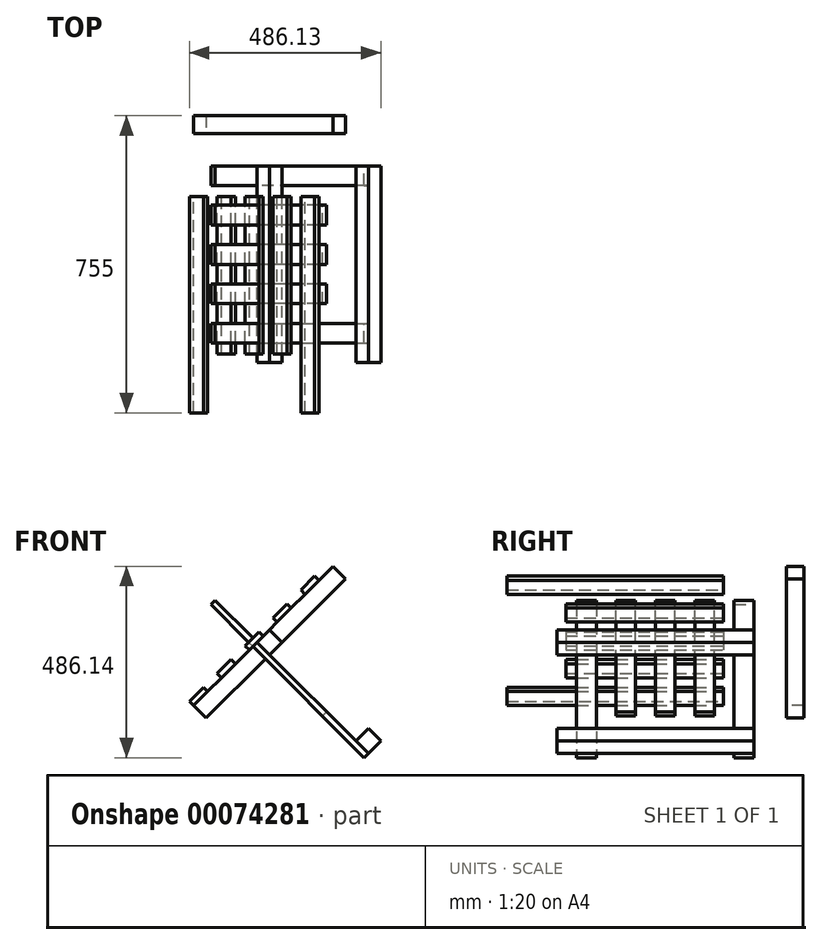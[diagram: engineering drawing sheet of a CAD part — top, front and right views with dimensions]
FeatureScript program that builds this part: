
annotation { "Feature Type Name" : "Feature", "Feature Type Description" : "" }
export const myFeature = defineFeature(function(context is Context, id is Id, definition is map)
    precondition{}
    {
        {
            var Q0;
            Q0=qCreatedBy(makeId("Front.planeOp"),FACE);
            var sketch = newSketch(context, id + "F0", { "sketchPlane" : qUnion([Q0])});
            skLineSegment(sketch, "E0.rect.bottom", {"start": v(0, 31.82) * mm, "end": v(31.82, 0) * mm});
            skLineSegment(sketch, "E0.rect.top", {"start": v(-31.82, 0) * mm, "end": v(0, -31.82) * mm});
            skLineSegment(sketch, "E0.rect.left", {"start": v(0, 31.82) * mm, "end": v(-31.82, 0) * mm});
            skLineSegment(sketch, "E0.rect.right", {"start": v(31.82, 0) * mm, "end": v(0, -31.82) * mm});
            skPoint(sketch, "E0.rect.middle", {"position": v(0, 0) * mm});
            skLineSegment(sketch, "E1", {"start": v(-57.8, 0) * mm, "end": v(51.56, 0) * mm, "construction": true});
            skSolve(sketch);
        }
        {
            var Q0;
            Q0=makeQuery(id+"F0.imprint","IMPRINT",FACE,{"disambiguationData":[TD([[makeQuery(id+"F0.imprint","IMPRINT",EDGE,{"derivedFrom":sQuery(id+"F0.wireOp",EDGE,"E0.rect.bottom")}),-1.0]])]});
            extrude(context, id + "F1", {"entities" : qUnion([Q0]), "endBound" : BoundingType.SYMMETRIC, "depth" : 500 * mm});
        }
        {
            var Q0;
            Q0=makeQuery(id+"F1.opExtrude","SWEPT_FACE",FACE,{"disambiguationData":[OSD([sQuery(id+"F0.wireOp",EDGE,"E0.rect.left")])]});
            var sketch = newSketch(context, id + "F2", { "sketchPlane" : qUnion([Q0])});
            skLineSegment(sketch, "E2.bottom", {"start": v(227.5, -200) * mm, "end": v(-172.5, -200) * mm});
            skLineSegment(sketch, "E2.top", {"start": v(227.5, -250) * mm, "end": v(-172.5, -250) * mm});
            skLineSegment(sketch, "E2.left", {"start": v(227.5, -200) * mm, "end": v(227.5, -250) * mm});
            skLineSegment(sketch, "E2.right", {"start": v(-172.5, -200) * mm, "end": v(-172.5, -250) * mm});
            skLineSegment(sketch, "E3.0.1.0", {"start": v(-172.5, -100) * mm, "end": v(-172.5, -150) * mm});
            skLineSegment(sketch, "E3.0.1.1", {"start": v(227.5, -100) * mm, "end": v(227.5, -150) * mm});
            skLineSegment(sketch, "E3.0.1.2", {"start": v(227.5, -150) * mm, "end": v(-172.5, -150) * mm});
            skLineSegment(sketch, "E3.0.1.3", {"start": v(227.5, -100) * mm, "end": v(-172.5, -100) * mm});
            skLineSegment(sketch, "E3.0.2.0", {"start": v(-172.5, 0) * mm, "end": v(-172.5, -50) * mm});
            skLineSegment(sketch, "E3.0.2.1", {"start": v(227.5, 0) * mm, "end": v(227.5, -50) * mm});
            skLineSegment(sketch, "E3.0.2.2", {"start": v(227.5, -50) * mm, "end": v(-172.5, -50) * mm});
            skLineSegment(sketch, "E3.0.2.3", {"start": v(227.5, 0) * mm, "end": v(-172.5, 0) * mm});
            skLineSegment(sketch, "E3.0.3.0", {"start": v(-172.5, 100) * mm, "end": v(-172.5, 50) * mm});
            skLineSegment(sketch, "E3.0.3.1", {"start": v(227.5, 100) * mm, "end": v(227.5, 50) * mm});
            skLineSegment(sketch, "E3.0.3.2", {"start": v(227.5, 50) * mm, "end": v(-172.5, 50) * mm});
            skLineSegment(sketch, "E3.0.3.3", {"start": v(227.5, 100) * mm, "end": v(-172.5, 100) * mm});
            skLineSegment(sketch, "E3.0.4.0", {"start": v(-172.5, 200) * mm, "end": v(-172.5, 150) * mm});
            skLineSegment(sketch, "E3.0.4.1", {"start": v(227.5, 200) * mm, "end": v(227.5, 150) * mm});
            skLineSegment(sketch, "E3.0.4.2", {"start": v(227.5, 150) * mm, "end": v(-172.5, 150) * mm});
            skLineSegment(sketch, "E3.0.4.3", {"start": v(227.5, 200) * mm, "end": v(-172.5, 200) * mm});
            skLineSegment(sketch, "E3.direction1", {"start": v(-172.5, -250) * mm, "end": v(-172.5, -250) * mm});
            skLineSegment(sketch, "E3.direction2", {"start": v(-172.5, -250) * mm, "end": v(-172.5, -150) * mm, "construction": true});
            skLineSegment(sketch, "E4.bottom", {"start": v(227.5, -200) * mm, "end": v(377.5, -200) * mm});
            skLineSegment(sketch, "E4.top", {"start": v(227.5, -250) * mm, "end": v(377.5, -250) * mm});
            skLineSegment(sketch, "E4.right", {"start": v(377.5, -200) * mm, "end": v(377.5, -250) * mm});
            skLineSegment(sketch, "E5.bottom", {"start": v(227.5, 200) * mm, "end": v(377.5, 200) * mm});
            skLineSegment(sketch, "E5.top", {"start": v(227.5, 150) * mm, "end": v(377.5, 150) * mm});
            skLineSegment(sketch, "E5.right", {"start": v(377.5, 200) * mm, "end": v(377.5, 150) * mm});
            skSolve(sketch);
        }
        {
            var Q0;
            {var subQ0=sQuery(id+"F2.wireOp",EDGE,"E2.left");Q0=makeQuery(id+"F2.imprint","IMPRINT",FACE,{"disambiguationData":[TD([[makeQuery(id+"F2.imprint","IMPRINT",EDGE,{"derivedFrom":subQ0}),-1.0]])]});}
            var Q1;
            Q1=makeQuery(id+"F2.imprint","IMPRINT",FACE,{"disambiguationData":[TD([[makeQuery(id+"F2.imprint","IMPRINT",EDGE,{"derivedFrom":sQuery(id+"F2.wireOp",EDGE,"E4.bottom")}),-1.0]])]});
            var Q2;
            {var subQ0=sQuery(id+"F2.wireOp",EDGE,"E2.right");Q2=makeQuery(id+"F2.imprint","IMPRINT",FACE,{"disambiguationData":[TD([[makeQuery(id+"F2.imprint","IMPRINT",EDGE,{"derivedFrom":subQ0}),1.0]])]});}
            var Q3;
            {var subQ0=sQuery(id+"F2.wireOp",EDGE,"E2.bottom");var subQ1=sQuery(id+"F0.wireOp",EDGE,"E0.rect.left");var subQ2=makeQuery(id+"F1.opExtrude","SWEPT_EDGE",EDGE,{"disambiguationData":[OSD([sQuery(id+"F0.wireOp",EDGE,"E0.rect.bottom"),subQ1])]});var subQ3=makeQuery(id+"F2.imprint","INTERSECT",VERTEX,{"derivedFrom":[subQ2,subQ0]});Q3=makeQuery(id+"F2.imprint","IMPRINT",FACE,{"disambiguationData":[TD([[makeQuery(id+"F2.imprint","IMPRINT",EDGE,{"disambiguationData":[TD([[subQ3,-1.0]])],"derivedFrom":subQ0}),1.0]])]});}
            var Q4;
            {var subQ0=sQuery(id+"F2.wireOp",EDGE,"E3.0.1.2");var subQ1=sQuery(id+"F0.wireOp",EDGE,"E0.rect.left");var subQ2=makeQuery(id+"F1.opExtrude","SWEPT_EDGE",EDGE,{"disambiguationData":[OSD([sQuery(id+"F0.wireOp",EDGE,"E0.rect.bottom"),subQ1])]});var subQ3=makeQuery(id+"F2.imprint","INTERSECT",VERTEX,{"derivedFrom":[subQ2,subQ0]});Q4=makeQuery(id+"F2.imprint","IMPRINT",FACE,{"disambiguationData":[TD([[makeQuery(id+"F2.imprint","IMPRINT",EDGE,{"disambiguationData":[TD([[subQ3,-1.0]])],"derivedFrom":subQ0}),-1.0]])]});}
            var Q5;
            {var subQ0=sQuery(id+"F2.wireOp",EDGE,"E3.0.2.2");var subQ1=sQuery(id+"F0.wireOp",EDGE,"E0.rect.left");var subQ2=makeQuery(id+"F1.opExtrude","SWEPT_EDGE",EDGE,{"disambiguationData":[OSD([sQuery(id+"F0.wireOp",EDGE,"E0.rect.bottom"),subQ1])]});var subQ3=makeQuery(id+"F2.imprint","INTERSECT",VERTEX,{"derivedFrom":[subQ2,subQ0]});Q5=makeQuery(id+"F2.imprint","IMPRINT",FACE,{"disambiguationData":[TD([[makeQuery(id+"F2.imprint","IMPRINT",EDGE,{"disambiguationData":[TD([[subQ3,-1.0]])],"derivedFrom":subQ0}),-1.0]])]});}
            var Q6;
            {var subQ0=sQuery(id+"F2.wireOp",EDGE,"E3.0.3.2");var subQ1=sQuery(id+"F0.wireOp",EDGE,"E0.rect.left");var subQ2=makeQuery(id+"F1.opExtrude","SWEPT_EDGE",EDGE,{"disambiguationData":[OSD([sQuery(id+"F0.wireOp",EDGE,"E0.rect.bottom"),subQ1])]});var subQ3=makeQuery(id+"F2.imprint","INTERSECT",VERTEX,{"derivedFrom":[subQ2,subQ0]});Q6=makeQuery(id+"F2.imprint","IMPRINT",FACE,{"disambiguationData":[TD([[makeQuery(id+"F2.imprint","IMPRINT",EDGE,{"disambiguationData":[TD([[subQ3,-1.0]])],"derivedFrom":subQ0}),-1.0]])]});}
            var Q7;
            {var subQ0=sQuery(id+"F2.wireOp",EDGE,"E3.0.4.2");var subQ1=sQuery(id+"F0.wireOp",EDGE,"E0.rect.left");var subQ2=makeQuery(id+"F1.opExtrude","SWEPT_EDGE",EDGE,{"disambiguationData":[OSD([sQuery(id+"F0.wireOp",EDGE,"E0.rect.bottom"),subQ1])]});var subQ3=makeQuery(id+"F2.imprint","INTERSECT",VERTEX,{"derivedFrom":[subQ2,subQ0]});Q7=makeQuery(id+"F2.imprint","IMPRINT",FACE,{"disambiguationData":[TD([[makeQuery(id+"F2.imprint","IMPRINT",EDGE,{"disambiguationData":[TD([[subQ3,-1.0]])],"derivedFrom":subQ0}),-1.0]])]});}
            var Q8;
            {var subQ0=sQuery(id+"F2.wireOp",EDGE,"E3.0.4.1");Q8=makeQuery(id+"F2.imprint","IMPRINT",FACE,{"disambiguationData":[TD([[makeQuery(id+"F2.imprint","IMPRINT",EDGE,{"derivedFrom":subQ0}),-1.0]])]});}
            var Q9;
            {var subQ0=sQuery(id+"F2.wireOp",EDGE,"E3.0.3.1");Q9=makeQuery(id+"F2.imprint","IMPRINT",FACE,{"disambiguationData":[TD([[makeQuery(id+"F2.imprint","IMPRINT",EDGE,{"derivedFrom":subQ0}),-1.0]])]});}
            var Q10;
            {var subQ0=sQuery(id+"F2.wireOp",EDGE,"E3.0.2.1");Q10=makeQuery(id+"F2.imprint","IMPRINT",FACE,{"disambiguationData":[TD([[makeQuery(id+"F2.imprint","IMPRINT",EDGE,{"derivedFrom":subQ0}),-1.0]])]});}
            var Q11;
            {var subQ0=sQuery(id+"F2.wireOp",EDGE,"E3.0.1.1");Q11=makeQuery(id+"F2.imprint","IMPRINT",FACE,{"disambiguationData":[TD([[makeQuery(id+"F2.imprint","IMPRINT",EDGE,{"derivedFrom":subQ0}),-1.0]])]});}
            var Q12;
            {var subQ0=sQuery(id+"F2.wireOp",EDGE,"E3.0.1.0");Q12=makeQuery(id+"F2.imprint","IMPRINT",FACE,{"disambiguationData":[TD([[makeQuery(id+"F2.imprint","IMPRINT",EDGE,{"derivedFrom":subQ0}),1.0]])]});}
            var Q13;
            {var subQ0=sQuery(id+"F2.wireOp",EDGE,"E3.0.2.0");Q13=makeQuery(id+"F2.imprint","IMPRINT",FACE,{"disambiguationData":[TD([[makeQuery(id+"F2.imprint","IMPRINT",EDGE,{"derivedFrom":subQ0}),1.0]])]});}
            var Q14;
            {var subQ0=sQuery(id+"F2.wireOp",EDGE,"E3.0.3.0");Q14=makeQuery(id+"F2.imprint","IMPRINT",FACE,{"disambiguationData":[TD([[makeQuery(id+"F2.imprint","IMPRINT",EDGE,{"derivedFrom":subQ0}),1.0]])]});}
            var Q15;
            {var subQ0=sQuery(id+"F2.wireOp",EDGE,"E3.0.4.0");Q15=makeQuery(id+"F2.imprint","IMPRINT",FACE,{"disambiguationData":[TD([[makeQuery(id+"F2.imprint","IMPRINT",EDGE,{"derivedFrom":subQ0}),1.0]])]});}
            var Q16;
            {var subQ0=sQuery(id+"F2.wireOp",EDGE,"E3.0.4.1");Q16=makeQuery(id+"F2.imprint","IMPRINT",FACE,{"disambiguationData":[TD([[makeQuery(id+"F2.imprint","IMPRINT",EDGE,{"derivedFrom":subQ0}),-1.0]])]});}
            var Q17;
            Q17=makeQuery(id+"F2.imprint","IMPRINT",FACE,{"disambiguationData":[TD([[makeQuery(id+"F2.imprint","IMPRINT",EDGE,{"derivedFrom":sQuery(id+"F2.wireOp",EDGE,"E5.bottom")}),-1.0]])]});
            extrude(context, id + "F3", {"entities" : qUnion([Q0, Q1, Q2, Q3, Q4, Q5, Q6, Q7, Q8, Q9, Q10, Q11, Q12, Q13, Q14, Q15, Q16, Q17]), "depth" : 15 * mm});
        }
        {
            var Q0;
            Q0=makeQuery(id+"F1.opExtrude","SWEPT_FACE",FACE,{"disambiguationData":[OSD([sQuery(id+"F0.wireOp",EDGE,"E0.rect.top")])]});
            var sketch = newSketch(context, id + "F4", { "sketchPlane" : qUnion([Q0])});
            skLineSegment(sketch, "E6.bottom", {"start": v(-200, -227.5) * mm, "end": v(-250, -227.5) * mm});
            skLineSegment(sketch, "E6.top", {"start": v(-200, 172.5) * mm, "end": v(-250, 172.5) * mm});
            skLineSegment(sketch, "E6.left", {"start": v(-200, -227.5) * mm, "end": v(-200, 172.5) * mm});
            skLineSegment(sketch, "E6.right", {"start": v(-250, -227.5) * mm, "end": v(-250, 172.5) * mm});
            skLineSegment(sketch, "E7.1.0.0", {"start": v(-100, -227.5) * mm, "end": v(-100, 172.5) * mm});
            skLineSegment(sketch, "E7.1.0.1", {"start": v(-150, -227.5) * mm, "end": v(-150, 172.5) * mm});
            skLineSegment(sketch, "E7.1.0.2", {"start": v(-100, -227.5) * mm, "end": v(-150, -227.5) * mm});
            skLineSegment(sketch, "E7.1.0.3", {"start": v(-100, 172.5) * mm, "end": v(-150, 172.5) * mm});
            skLineSegment(sketch, "E7.2.0.0", {"start": v(0, -227.5) * mm, "end": v(0, 172.5) * mm});
            skLineSegment(sketch, "E7.2.0.1", {"start": v(-50, -227.5) * mm, "end": v(-50, 172.5) * mm});
            skLineSegment(sketch, "E7.2.0.2", {"start": v(0, -227.5) * mm, "end": v(-50, -227.5) * mm});
            skLineSegment(sketch, "E7.2.0.3", {"start": v(0, 172.5) * mm, "end": v(-50, 172.5) * mm});
            skLineSegment(sketch, "E7.3.0.0", {"start": v(100, -227.5) * mm, "end": v(100, 172.5) * mm});
            skLineSegment(sketch, "E7.3.0.1", {"start": v(50, -227.5) * mm, "end": v(50, 172.5) * mm});
            skLineSegment(sketch, "E7.3.0.2", {"start": v(100, -227.5) * mm, "end": v(50, -227.5) * mm});
            skLineSegment(sketch, "E7.3.0.3", {"start": v(100, 172.5) * mm, "end": v(50, 172.5) * mm});
            skLineSegment(sketch, "E7.4.0.0", {"start": v(200, -227.5) * mm, "end": v(200, 172.5) * mm});
            skLineSegment(sketch, "E7.4.0.1", {"start": v(150, -227.5) * mm, "end": v(150, 172.5) * mm});
            skLineSegment(sketch, "E7.4.0.2", {"start": v(200, -227.5) * mm, "end": v(150, -227.5) * mm});
            skLineSegment(sketch, "E7.4.0.3", {"start": v(200, 172.5) * mm, "end": v(150, 172.5) * mm});
            skLineSegment(sketch, "E7.direction1", {"start": v(-200, -227.5) * mm, "end": v(-100, -227.5) * mm, "construction": true});
            skLineSegment(sketch, "E8.top", {"start": v(-200, -377.5) * mm, "end": v(-250, -377.5) * mm});
            skLineSegment(sketch, "E8.left", {"start": v(-200, -227.5) * mm, "end": v(-200, -377.5) * mm});
            skLineSegment(sketch, "E8.right", {"start": v(-250, -227.5) * mm, "end": v(-250, -377.5) * mm});
            skLineSegment(sketch, "E9.top", {"start": v(200, -377.5) * mm, "end": v(150, -377.5) * mm});
            skLineSegment(sketch, "E9.left", {"start": v(200, -227.5) * mm, "end": v(200, -377.5) * mm});
            skLineSegment(sketch, "E9.right", {"start": v(150, -227.5) * mm, "end": v(150, -377.5) * mm});
            skSolve(sketch);
        }
        {
            var Q0;
            Q0=makeQuery(id+"F4.imprint","IMPRINT",FACE,{"disambiguationData":[TD([[makeQuery(id+"F4.imprint","IMPRINT",EDGE,{"derivedFrom":sQuery(id+"F4.wireOp",EDGE,"E7.4.0.2")}),1.0]])]});
            var Q1;
            {var subQ0=sQuery(id+"F4.wireOp",EDGE,"E7.4.0.2");Q1=makeQuery(id+"F4.imprint","IMPRINT",FACE,{"disambiguationData":[TD([[makeQuery(id+"F4.imprint","IMPRINT",EDGE,{"derivedFrom":subQ0}),-1.0]])]});}
            var Q2;
            {var subQ0=sQuery(id+"F4.wireOp",EDGE,"E7.4.0.0");var subQ1=sQuery(id+"F0.wireOp",EDGE,"E0.rect.top");var subQ2=makeQuery(id+"F1.opExtrude","SWEPT_EDGE",EDGE,{"disambiguationData":[OSD([subQ1,sQuery(id+"F0.wireOp",EDGE,"E0.rect.right")])]});var subQ3=makeQuery(id+"F4.imprint","INTERSECT",VERTEX,{"derivedFrom":[subQ2,subQ0]});Q2=makeQuery(id+"F4.imprint","IMPRINT",FACE,{"disambiguationData":[TD([[makeQuery(id+"F4.imprint","IMPRINT",EDGE,{"disambiguationData":[TD([[subQ3,-1.0]])],"derivedFrom":subQ0}),1.0]])]});}
            var Q3;
            {var subQ0=sQuery(id+"F4.wireOp",EDGE,"E7.4.0.3");Q3=makeQuery(id+"F4.imprint","IMPRINT",FACE,{"disambiguationData":[TD([[makeQuery(id+"F4.imprint","IMPRINT",EDGE,{"derivedFrom":subQ0}),1.0]])]});}
            var Q4;
            {var subQ0=sQuery(id+"F4.wireOp",EDGE,"E7.3.0.3");Q4=makeQuery(id+"F4.imprint","IMPRINT",FACE,{"disambiguationData":[TD([[makeQuery(id+"F4.imprint","IMPRINT",EDGE,{"derivedFrom":subQ0}),1.0]])]});}
            var Q5;
            {var subQ0=sQuery(id+"F4.wireOp",EDGE,"E7.3.0.0");var subQ1=sQuery(id+"F0.wireOp",EDGE,"E0.rect.top");var subQ2=makeQuery(id+"F1.opExtrude","SWEPT_EDGE",EDGE,{"disambiguationData":[OSD([subQ1,sQuery(id+"F0.wireOp",EDGE,"E0.rect.right")])]});var subQ3=makeQuery(id+"F4.imprint","INTERSECT",VERTEX,{"derivedFrom":[subQ2,subQ0]});Q5=makeQuery(id+"F4.imprint","IMPRINT",FACE,{"disambiguationData":[TD([[makeQuery(id+"F4.imprint","IMPRINT",EDGE,{"disambiguationData":[TD([[subQ3,-1.0]])],"derivedFrom":subQ0}),1.0]])]});}
            var Q6;
            {var subQ0=sQuery(id+"F4.wireOp",EDGE,"E7.3.0.2");Q6=makeQuery(id+"F4.imprint","IMPRINT",FACE,{"disambiguationData":[TD([[makeQuery(id+"F4.imprint","IMPRINT",EDGE,{"derivedFrom":subQ0}),-1.0]])]});}
            var Q7;
            {var subQ0=sQuery(id+"F4.wireOp",EDGE,"E7.2.0.2");Q7=makeQuery(id+"F4.imprint","IMPRINT",FACE,{"disambiguationData":[TD([[makeQuery(id+"F4.imprint","IMPRINT",EDGE,{"derivedFrom":subQ0}),-1.0]])]});}
            var Q8;
            {var subQ0=sQuery(id+"F4.wireOp",EDGE,"E7.2.0.0");var subQ1=sQuery(id+"F0.wireOp",EDGE,"E0.rect.top");var subQ2=makeQuery(id+"F1.opExtrude","SWEPT_EDGE",EDGE,{"disambiguationData":[OSD([subQ1,sQuery(id+"F0.wireOp",EDGE,"E0.rect.right")])]});var subQ3=makeQuery(id+"F4.imprint","INTERSECT",VERTEX,{"derivedFrom":[subQ2,subQ0]});Q8=makeQuery(id+"F4.imprint","IMPRINT",FACE,{"disambiguationData":[TD([[makeQuery(id+"F4.imprint","IMPRINT",EDGE,{"disambiguationData":[TD([[subQ3,-1.0]])],"derivedFrom":subQ0}),1.0]])]});}
            var Q9;
            {var subQ0=sQuery(id+"F4.wireOp",EDGE,"E7.2.0.3");Q9=makeQuery(id+"F4.imprint","IMPRINT",FACE,{"disambiguationData":[TD([[makeQuery(id+"F4.imprint","IMPRINT",EDGE,{"derivedFrom":subQ0}),1.0]])]});}
            var Q10;
            {var subQ0=sQuery(id+"F4.wireOp",EDGE,"E7.1.0.2");Q10=makeQuery(id+"F4.imprint","IMPRINT",FACE,{"disambiguationData":[TD([[makeQuery(id+"F4.imprint","IMPRINT",EDGE,{"derivedFrom":subQ0}),-1.0]])]});}
            var Q11;
            {var subQ0=sQuery(id+"F4.wireOp",EDGE,"E7.1.0.0");var subQ1=sQuery(id+"F0.wireOp",EDGE,"E0.rect.top");var subQ2=makeQuery(id+"F1.opExtrude","SWEPT_EDGE",EDGE,{"disambiguationData":[OSD([subQ1,sQuery(id+"F0.wireOp",EDGE,"E0.rect.right")])]});var subQ3=makeQuery(id+"F4.imprint","INTERSECT",VERTEX,{"derivedFrom":[subQ2,subQ0]});Q11=makeQuery(id+"F4.imprint","IMPRINT",FACE,{"disambiguationData":[TD([[makeQuery(id+"F4.imprint","IMPRINT",EDGE,{"disambiguationData":[TD([[subQ3,-1.0]])],"derivedFrom":subQ0}),1.0]])]});}
            var Q12;
            {var subQ0=sQuery(id+"F4.wireOp",EDGE,"E7.1.0.3");Q12=makeQuery(id+"F4.imprint","IMPRINT",FACE,{"disambiguationData":[TD([[makeQuery(id+"F4.imprint","IMPRINT",EDGE,{"derivedFrom":subQ0}),1.0]])]});}
            var Q13;
            {var subQ0=sQuery(id+"F4.wireOp",EDGE,"E6.top");Q13=makeQuery(id+"F4.imprint","IMPRINT",FACE,{"disambiguationData":[TD([[makeQuery(id+"F4.imprint","IMPRINT",EDGE,{"derivedFrom":subQ0}),1.0]])]});}
            var Q14;
            {var subQ0=sQuery(id+"F4.wireOp",EDGE,"E6.left");var subQ1=sQuery(id+"F0.wireOp",EDGE,"E0.rect.top");var subQ2=makeQuery(id+"F1.opExtrude","SWEPT_EDGE",EDGE,{"disambiguationData":[OSD([subQ1,sQuery(id+"F0.wireOp",EDGE,"E0.rect.right")])]});var subQ3=makeQuery(id+"F4.imprint","INTERSECT",VERTEX,{"derivedFrom":[subQ2,subQ0]});Q14=makeQuery(id+"F4.imprint","IMPRINT",FACE,{"disambiguationData":[TD([[makeQuery(id+"F4.imprint","IMPRINT",EDGE,{"disambiguationData":[TD([[subQ3,-1.0]])],"derivedFrom":subQ0}),1.0]])]});}
            var Q15;
            {var subQ0=sQuery(id+"F4.wireOp",EDGE,"E6.bottom");Q15=makeQuery(id+"F4.imprint","IMPRINT",FACE,{"disambiguationData":[TD([[makeQuery(id+"F4.imprint","IMPRINT",EDGE,{"derivedFrom":subQ0}),-1.0]])]});}
            var Q16;
            Q16=makeQuery(id+"F4.imprint","IMPRINT",FACE,{"disambiguationData":[TD([[makeQuery(id+"F4.imprint","IMPRINT",EDGE,{"derivedFrom":sQuery(id+"F4.wireOp",EDGE,"E6.bottom")}),1.0]])]});
            extrude(context, id + "F5", {"entities" : qUnion([Q0, Q1, Q2, Q3, Q4, Q5, Q6, Q7, Q8, Q9, Q10, Q11, Q12, Q13, Q14, Q15, Q16]), "depth" : 15 * mm});
        }
        {
            var Q0;
            Q0=makeQuery(id+"F5.opExtrude","CAP_FACE",FACE,{"disambiguationData":[OSD([sQuery(id+"F4.wireOp",EDGE,"E6.top"),sQuery(id+"F4.wireOp",EDGE,"E6.left"),sQuery(id+"F4.wireOp",EDGE,"E6.right"),sQuery(id+"F4.wireOp",EDGE,"E8.top"),sQuery(id+"F4.wireOp",EDGE,"E8.left"),sQuery(id+"F4.wireOp",EDGE,"E8.right")])],"isStart":true});
            var sketch = newSketch(context, id + "F6", { "sketchPlane" : qUnion([Q0])});
            skLineSegment(sketch, "E10.bottom", {"start": v(250, -377.5) * mm, "end": v(-250, -377.5) * mm});
            skLineSegment(sketch, "E10.top", {"start": v(250, -332.5) * mm, "end": v(-250, -332.5) * mm});
            skLineSegment(sketch, "E10.left", {"start": v(250, -377.5) * mm, "end": v(250, -332.5) * mm});
            skLineSegment(sketch, "E10.right", {"start": v(-250, -377.5) * mm, "end": v(-250, -332.5) * mm});
            skSolve(sketch);
        }
        {
            var Q0;
            {var subQ3=sQuery(id+"F6.wireOp",EDGE,"E10.right");Q0=makeQuery(id+"F6.imprint","IMPRINT",FACE,{"disambiguationData":[TD([[makeQuery(id+"F6.imprint","IMPRINT",EDGE,{"derivedFrom":subQ3}),-1.0]])]});}
            var Q1;
            {var subQ3=sQuery(id+"F6.wireOp",EDGE,"E10.left");Q1=makeQuery(id+"F6.imprint","IMPRINT",FACE,{"disambiguationData":[TD([[makeQuery(id+"F6.imprint","IMPRINT",EDGE,{"derivedFrom":subQ3}),1.0]])]});}
            extrude(context, id + "F7", {"entities" : qUnion([Q0, Q1]), "depth" : 45 * mm});
        }
        {
            var Q0;
            Q0=makeQuery(id+"F3.opExtrude","CAP_FACE",FACE,{"disambiguationData":[OSD([sQuery(id+"F2.wireOp",EDGE,"E2.bottom"),sQuery(id+"F2.wireOp",EDGE,"E2.top"),sQuery(id+"F2.wireOp",EDGE,"E2.right"),sQuery(id+"F2.wireOp",EDGE,"E4.bottom"),sQuery(id+"F2.wireOp",EDGE,"E4.top"),sQuery(id+"F2.wireOp",EDGE,"E4.right")])],"isStart":true});
            var sketch = newSketch(context, id + "F8", { "sketchPlane" : qUnion([Q0])});
            skLineSegment(sketch, "E11.bottom", {"start": v(377.5, 250) * mm, "end": v(332.5, 250) * mm});
            skLineSegment(sketch, "E11.top", {"start": v(377.5, -250) * mm, "end": v(332.5, -250) * mm});
            skLineSegment(sketch, "E11.left", {"start": v(377.5, 250) * mm, "end": v(377.5, -250) * mm});
            skLineSegment(sketch, "E11.right", {"start": v(332.5, 250) * mm, "end": v(332.5, -250) * mm});
            skSolve(sketch);
        }
        {
            var Q0;
            {var subQ0=sQuery(id+"F8.wireOp",EDGE,"E11.top");Q0=makeQuery(id+"F8.imprint","IMPRINT",FACE,{"disambiguationData":[TD([[makeQuery(id+"F8.imprint","IMPRINT",EDGE,{"derivedFrom":subQ0}),-1.0]])]});}
            var Q1;
            {var subQ0=sQuery(id+"F8.wireOp",EDGE,"E11.bottom");Q1=makeQuery(id+"F8.imprint","IMPRINT",FACE,{"disambiguationData":[TD([[makeQuery(id+"F8.imprint","IMPRINT",EDGE,{"derivedFrom":subQ0}),1.0]])]});}
            extrude(context, id + "F9", {"entities" : qUnion([Q0, Q1]), "depth" : 45 * mm});
        }
    });
